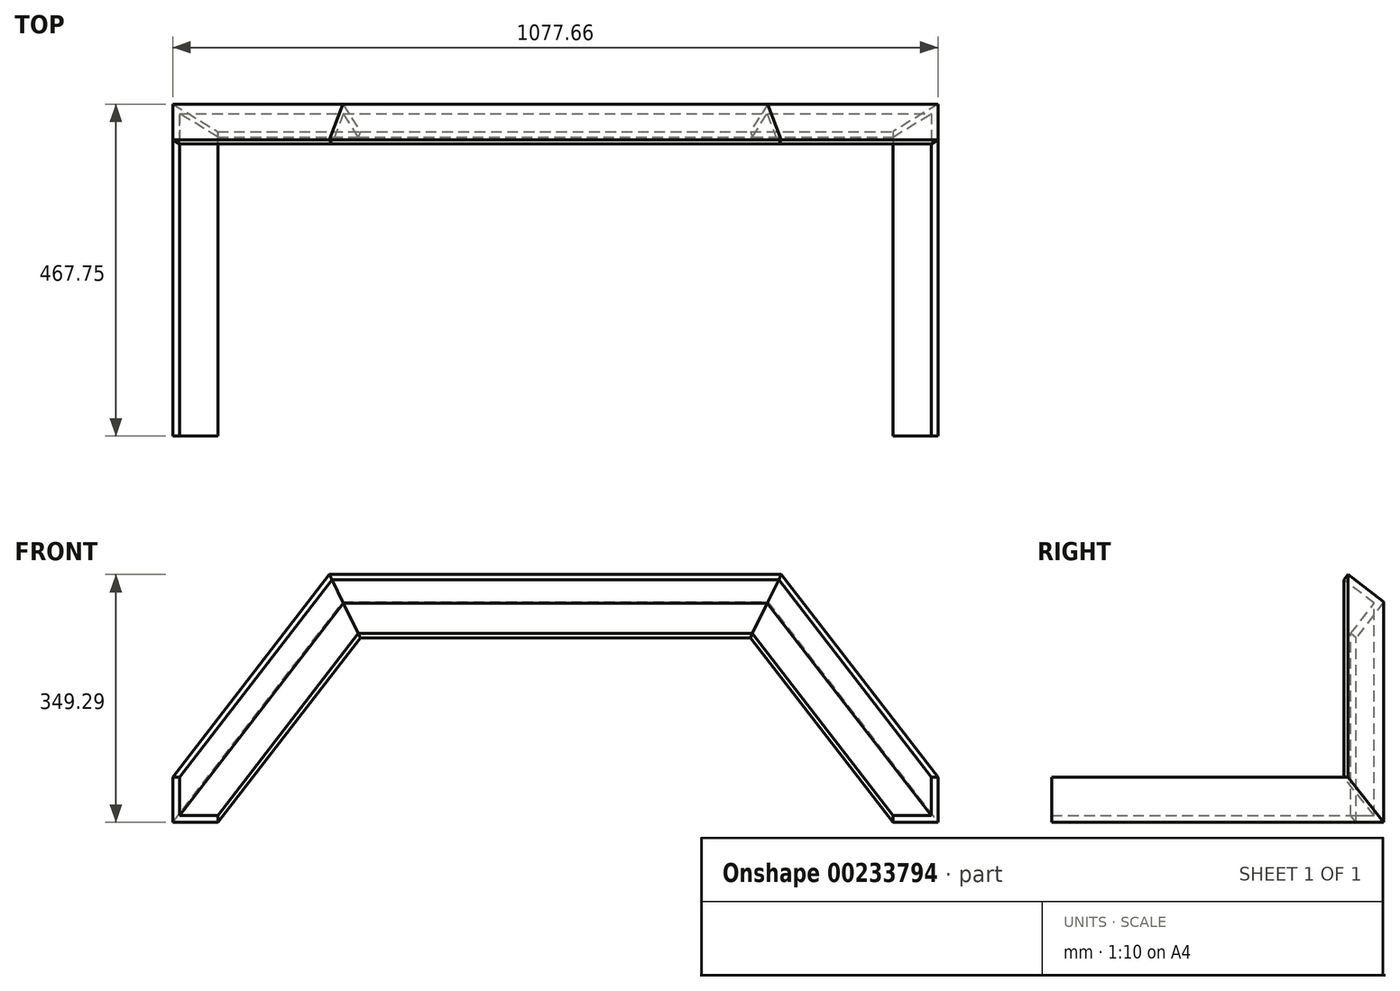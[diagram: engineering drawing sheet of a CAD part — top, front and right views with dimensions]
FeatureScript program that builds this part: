
annotation { "Feature Type Name" : "Feature", "Feature Type Description" : "" }
export const myFeature = defineFeature(function(context is Context, id is Id, definition is map)
    precondition{}
    {
        {
            var Q0;
            Q0=qCreatedBy(makeId("Front.planeOp"),FACE);
            var sketch = newSketch(context, id + "F0", { "sketchPlane" : qUnion([Q0])});
            skLineSegment(sketch, "E0", {"start": v(0, 0) * mm, "end": v(200.8, 260.23) * mm});
            skLineSegment(sketch, "E1", {"start": v(200.8, 260.23) * mm, "end": v(475.33, 260.23) * mm});
            skLineSegment(sketch, "E2", {"start": v(475.33, 260.23) * mm, "end": v(475.33, 0) * mm, "construction": true});
            skLineSegment(sketch, "E3.MirrorCS", {"start": v(950.66, 0) * mm, "end": v(749.87, 260.23) * mm});
            skLineSegment(sketch, "E4.MirrorCS", {"start": v(749.87, 260.23) * mm, "end": v(475.33, 260.23) * mm});
            skSolve(sketch);
        }
        {
            var Q0;
            Q0=qCreatedBy(makeId("Top.planeOp"),FACE);
            var sketch = newSketch(context, id + "F1", { "sketchPlane" : qUnion([Q0])});
            skPoint(sketch, "E5.0", {"position": v(0, 0) * mm});
            skPoint(sketch, "E6.0", {"position": v(950.66, 0) * mm});
            skLineSegment(sketch, "E7", {"start": v(0, 0) * mm, "end": v(0, -428.96) * mm});
            skLineSegment(sketch, "E8", {"start": v(950.66, 0) * mm, "end": v(950.66, -428.96) * mm});
            skSolve(sketch);
        }
        {
            var Q0;
            Q0=qCreatedBy(makeId("Front.planeOp"),FACE);
            var Q1;
            Q1=sQuery(id+"F1.wireOp",VERTEX,"E7.end");
            cPlane(context, id + "F2", {"entities" : qUnion([Q0, Q1]), "cplaneType" : CPlaneType.PLANE_POINT, "offset" : 25.4 * mm, "width" : 152.4 * mm, "height" : 152.4 * mm});
        }
        {
            var Q0;
            Q0=qCreatedBy(id+"F2.planeOp",FACE);
            var sketch = newSketch(context, id + "F3", { "sketchPlane" : qUnion([Q0])});
            skLineSegment(sketch, "E9.bottom", {"start": v(0, 0) * mm, "end": v(-63.5, 0) * mm});
            skLineSegment(sketch, "E9.top", {"start": v(0, 9.53) * mm, "end": v(-63.5, 9.53) * mm});
            skLineSegment(sketch, "E9.left", {"start": v(0, 0) * mm, "end": v(0, 9.53) * mm});
            skLineSegment(sketch, "E9.right", {"start": v(-63.5, 0) * mm, "end": v(-63.5, 9.53) * mm});
            skLineSegment(sketch, "E10.bottom", {"start": v(-63.5, 0) * mm, "end": v(-53.98, 0) * mm});
            skLineSegment(sketch, "E10.top", {"start": v(-63.5, 63.5) * mm, "end": v(-53.97, 63.5) * mm});
            skLineSegment(sketch, "E10.left", {"start": v(-63.5, 0) * mm, "end": v(-63.5, 63.5) * mm});
            skLineSegment(sketch, "E10.right", {"start": v(-53.98, 0) * mm, "end": v(-53.98, 63.5) * mm});
            skSolve(sketch);
        }
        {
            var Q0;
            {var subQ0=sQuery(id+"F3.wireOp",EDGE,"E9.bottom");Q0=makeQuery(id+"F3.imprint","IMPRINT",FACE,{"disambiguationData":[TD([[makeQuery(id+"F3.imprint","IMPRINT",EDGE,{"derivedFrom":subQ0}),-1.0]])]});}
            var Q1;
            {var subQ5=sQuery(id+"F3.wireOp",EDGE,"E10.top");Q1=makeQuery(id+"F3.imprint","IMPRINT",FACE,{"disambiguationData":[TD([[makeQuery(id+"F3.imprint","IMPRINT",EDGE,{"derivedFrom":subQ5}),-1.0]])]});}
            var Q2;
            {var subQ5=sQuery(id+"F3.wireOp",EDGE,"E10.bottom");Q2=makeQuery(id+"F3.imprint","IMPRINT",FACE,{"disambiguationData":[TD([[makeQuery(id+"F3.imprint","IMPRINT",EDGE,{"derivedFrom":subQ5}),1.0]])]});}
            var Q3;
            Q3=sQuery(id+"F1.wireOp",EDGE,"E7");
            var Q4;
            Q4=sQuery(id+"F0.wireOp",EDGE,"E0");
            var Q5;
            Q5=sQuery(id+"F0.wireOp",EDGE,"E1");
            var Q6;
            Q6=sQuery(id+"F0.wireOp",EDGE,"E4.MirrorCS");
            var Q7;
            Q7=sQuery(id+"F0.wireOp",EDGE,"E3.MirrorCS");
            var Q8;
            Q8=sQuery(id+"F1.wireOp",EDGE,"E8");
            sweep(context, id + "F4", {"profiles" : qUnion([Q0, Q1, Q2]), "path" : qUnion([Q3, Q4, Q5, Q6, Q7, Q8])});
        }
    });
